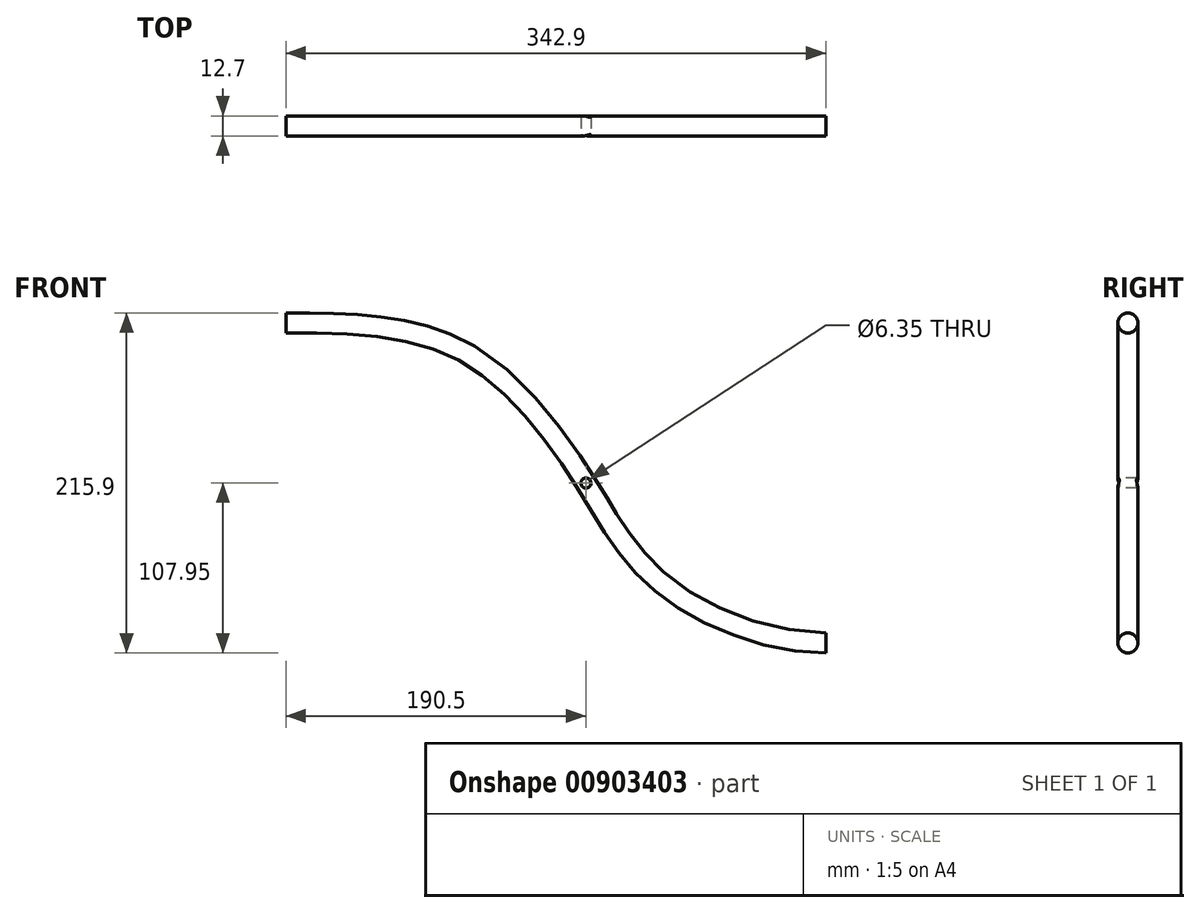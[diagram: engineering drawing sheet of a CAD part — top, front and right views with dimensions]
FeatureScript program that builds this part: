
annotation { "Feature Type Name" : "Feature", "Feature Type Description" : "" }
export const myFeature = defineFeature(function(context is Context, id is Id, definition is map)
    precondition{}
    {
        {
            var Q0;
            Q0=qCreatedBy(makeId("Front.planeOp"),FACE);
            var sketch = newSketch(context, id + "F0", { "sketchPlane" : qUnion([Q0])});
            skFitSpline(sketch, "E0", {"points": [v(0, 0) * mm, v(112.73, -18.03) * mm, v(190.5, -101.6) * mm, v(239.81, -166.56) * mm, v(342.9, -203.2) * mm], "startDerivative": vector(450.88, 0) * mm, "endDerivative": vector(427.16, 0) * mm});
            skLineSegment(sketch, "E1", {"start": v(0, 0) * mm, "end": v(112.73, -18.03) * mm, "construction": true});
            skLineSegment(sketch, "E2", {"start": v(112.73, -18.03) * mm, "end": v(190.5, -101.6) * mm, "construction": true});
            skCircle(sketch, "E3", {"center": v(190.5, -101.6) * mm, "radius": 3.18 * mm});
            skSolve(sketch);
        }
        {
            var Q0;
            Q0=qCreatedBy(makeId("Right.planeOp"),FACE);
            var sketch = newSketch(context, id + "F1", { "sketchPlane" : qUnion([Q0])});
            skCircle(sketch, "E4", {"center": v(0, 0) * mm, "radius": 6.35 * mm});
            skSolve(sketch);
        }
        {
            var Q0;
            Q0=makeQuery(id+"F1.imprint","IMPRINT",FACE,{"disambiguationData":[TD([[makeQuery(id+"F1.imprint","IMPRINT",EDGE,{"derivedFrom":sQuery(id+"F1.wireOp",EDGE,"E4")}),1.0]])]});
            var Q1;
            Q1=sQuery(id+"F0.wireOp",EDGE,"E0");
            sweep(context, id + "F2", {"profiles" : qUnion([Q0]), "path" : qUnion([Q1])});
        }
        {
            var Q0;
            Q0 = qSketchRegion(id + "F0", true);
            extrude(context, id + "F3", {"entities" : qUnion([Q0]), "operationType" : NewBodyOperationType.REMOVE, "endBound" : BoundingType.SYMMETRIC, "oppositeDirection" : true, "depth" : 25.4 * mm, "offsetDistance" : 25.4 * mm});
        }
    });
